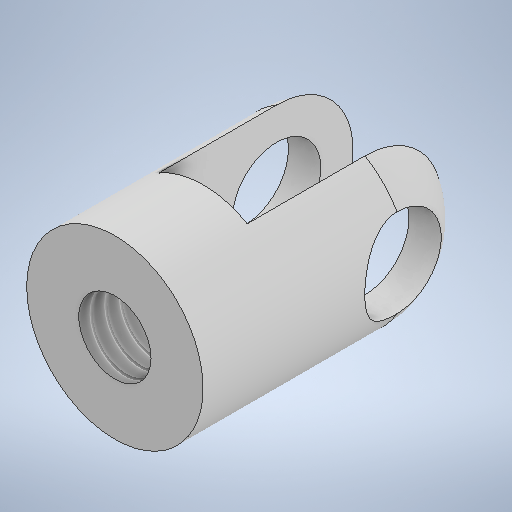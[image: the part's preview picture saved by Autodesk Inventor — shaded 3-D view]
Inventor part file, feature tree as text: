
AUTODESK INVENTOR PART (.ipt)
format: ipt  version: 2025.1 (Build 291241000, 241)  size: 308,736 bytes
history: native  units: mm
features: sketch x4, extrude x3, plane x2, fillet x1, hole x1, projected_geometry x1
ambient origin geometry x8: Origin, YZ Plane, XZ Plane, XY Plane, X Axis, Y Axis, Z Axis, Center Point
bodies: Solid1 (feature_tree)
feature tree (12):
  extrude  "Extrusion1"  Depth=10.0mm TaperAngle=0.0deg
  fillet  "Fillet1"  Radius=3.0mm
  plane  "Work Plane2"
  plane  "Work Plane3"
  extrude  "Extrusion4"  Depth=3.0mm TaperAngle=0.0deg
  extrude  "Extrusion3"  Depth=3.0mm
  hole  "Hole2"  [1 undecoded]
  sketch  "Sketch1"  dims[d0=6.0mm d1=10.0mm d2=0.0mm d15=3.0mm]
  sketch  "Sketch5"  dims[d16=3.0mm d18=6.0mm d19=0.0mm]
  projected_geometry  "Projected Loop1"
  sketch  "Sketch6"  dims[d20=3.0mm d21=3.0mm]
  sketch  "Sketch7"  dims[d22=3.0mm d23=6.0mm d24=0.0mm d25=7.0mm d26=1.5mm d27=2.459mm d28=6.0mm d29=4.0mm d30=2.0mm d31=90.0deg d32=8.0mm d33=0.0mm]
note: 1 required parameter value undecoded (feature->parameter linkage not recoverable at this tier; creation-order binding heuristic only, values carry confidence <= 0.55)
